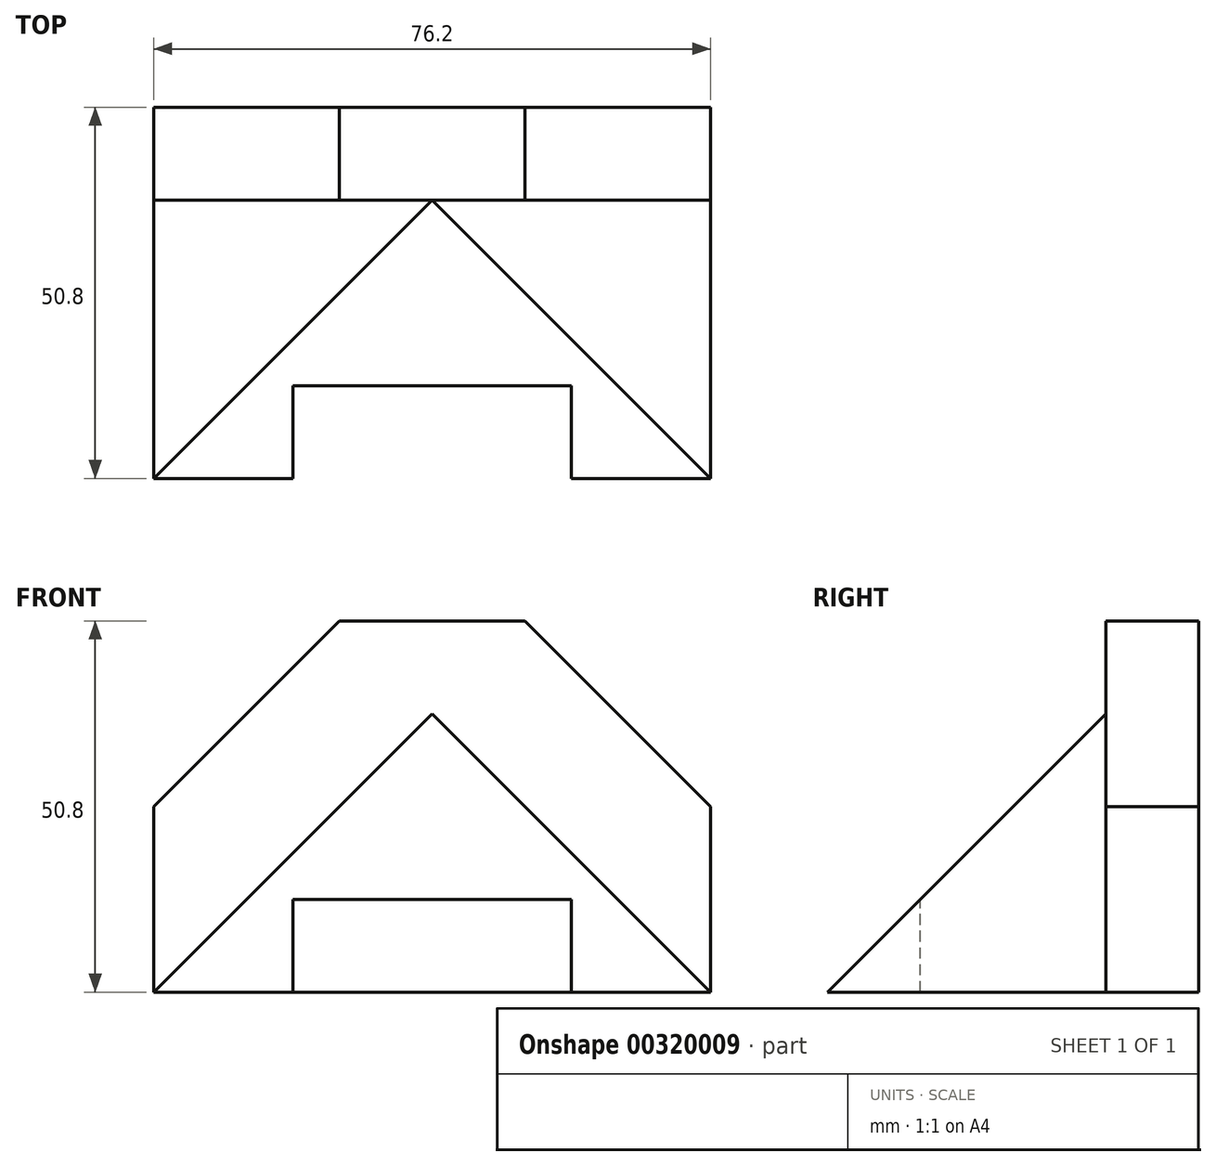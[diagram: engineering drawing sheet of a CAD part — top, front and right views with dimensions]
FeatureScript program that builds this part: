
annotation { "Feature Type Name" : "Feature", "Feature Type Description" : "" }
export const myFeature = defineFeature(function(context is Context, id is Id, definition is map)
    precondition{}
    {
        {
            var Q0;
            Q0=qCreatedBy(makeId("Front.planeOp"),FACE);
            var sketch = newSketch(context, id + "F0", { "sketchPlane" : qUnion([Q0])});
            skLineSegment(sketch, "E0.bottom", {"start": v(0, 0) * mm, "end": v(76.2, 0) * mm});
            skLineSegment(sketch, "E0.top", {"start": v(0, 50.8) * mm, "end": v(76.2, 50.8) * mm});
            skLineSegment(sketch, "E0.left", {"start": v(0, 0) * mm, "end": v(0, 50.8) * mm});
            skLineSegment(sketch, "E0.right", {"start": v(76.2, 0) * mm, "end": v(76.2, 50.8) * mm});
            skLineSegment(sketch, "E1", {"start": v(76.2, 0) * mm, "end": v(38.1, 38.1) * mm});
            skLineSegment(sketch, "E2", {"start": v(38.1, 38.1) * mm, "end": v(0, 0) * mm});
            skSolve(sketch);
        }
        {
            var Q0;
            Q0 = qSketchRegion(id + "F0", true);
            extrude(context, id + "F1", {"entities" : qUnion([Q0]), "oppositeDirection" : true, "depth" : 50.8 * mm});
        }
        {
            var Q0;
            Q0=makeQuery(id+"F1.opExtrude","SWEPT_FACE",FACE,{"disambiguationData":[OSD([sQuery(id+"F0.wireOp",EDGE,"E0.top")])]});
            var sketch = newSketch(context, id + "F2", { "sketchPlane" : qUnion([Q0])});
            skLineSegment(sketch, "E3", {"start": v(19.05, 0) * mm, "end": v(19.05, 12.7) * mm});
            skLineSegment(sketch, "E4", {"start": v(19.05, 12.7) * mm, "end": v(57.15, 12.7) * mm});
            skLineSegment(sketch, "E5", {"start": v(57.15, 12.7) * mm, "end": v(57.15, 0) * mm});
            skSolve(sketch);
        }
        {
            var Q0;
            {var subQ0=sQuery(id+"F2.wireOp",EDGE,"E3");Q0=makeQuery(id+"F2.imprint","IMPRINT",FACE,{"disambiguationData":[TD([[makeQuery(id+"F2.imprint","IMPRINT",EDGE,{"derivedFrom":subQ0}),-1.0]])]});}
            extrude(context, id + "F3", {"entities" : qUnion([Q0]), "operationType" : NewBodyOperationType.REMOVE, "oppositeDirection" : true, "depth" : 76.2 * mm});
        }
        {
            var Q0;
            {var subQ0=sQuery(id+"F0.wireOp",EDGE,"E0.right");Q0=makeQuery(id+"F0.imprint","IMPRINT",FACE,{"disambiguationData":[TD([[makeQuery(id+"F0.imprint","IMPRINT",EDGE,{"derivedFrom":subQ0}),1.0]])]});}
            var Q1;
            {var subQ0=sQuery(id+"F0.wireOp",EDGE,"E0.left");Q1=makeQuery(id+"F0.imprint","IMPRINT",FACE,{"disambiguationData":[TD([[makeQuery(id+"F0.imprint","IMPRINT",EDGE,{"derivedFrom":subQ0}),-1.0]])]});}
            extrude(context, id + "F4", {"entities" : qUnion([Q0, Q1]), "operationType" : NewBodyOperationType.REMOVE, "oppositeDirection" : true, "depth" : 38.1 * mm});
        }
        {
            var Q0;
            Q0=makeQuery(id+"F1.opExtrude","SWEPT_FACE",FACE,{"disambiguationData":[OSD([sQuery(id+"F0.wireOp",EDGE,"E0.right")])]});
            var sketch = newSketch(context, id + "F5", { "sketchPlane" : qUnion([Q0])});
            skLineSegment(sketch, "E6", {"start": v(38.1, 38.1) * mm, "end": v(0, 0) * mm});
            skLineSegment(sketch, "E7", {"start": v(38.1, 50.8) * mm, "end": v(12.7, 50.8) * mm});
            skLineSegment(sketch, "E8", {"start": v(12.7, 50.8) * mm, "end": v(12.7, 25.4) * mm});
            skLineSegment(sketch, "E9", {"start": v(12.7, 25.4) * mm, "end": v(0, 25.4) * mm});
            skLineSegment(sketch, "E10", {"start": v(0, 25.4) * mm, "end": v(0, 0) * mm});
            skSolve(sketch);
        }
        {
            var Q0;
            {var subQ1=sQuery(id+"F5.wireOp",EDGE,"E6");Q0=makeQuery(id+"F5.imprint","IMPRINT",FACE,{"disambiguationData":[TD([[makeQuery(id+"F5.imprint","IMPRINT",EDGE,{"derivedFrom":subQ1}),-1.0]])]});}
            extrude(context, id + "F6", {"entities" : qUnion([Q0]), "operationType" : NewBodyOperationType.REMOVE, "oppositeDirection" : true, "depth" : 101.6 * mm});
        }
        {
            var Q0;
            Q0=makeQuery(id+"F4.boolean.opBoolean","COPY",FACE,{"derivedFrom":makeQuery(id+"F4.opExtrude","CAP_FACE",FACE,{"disambiguationData":[OSD([sQuery(id+"F0.wireOp",EDGE,"E0.top"),sQuery(id+"F0.wireOp",EDGE,"E0.left"),sQuery(id+"F0.wireOp",EDGE,"E0.right"),sQuery(id+"F0.wireOp",EDGE,"E1"),sQuery(id+"F0.wireOp",EDGE,"E2")])],"isStart":false})});
            var sketch = newSketch(context, id + "F7", { "sketchPlane" : qUnion([Q0])});
            skLineSegment(sketch, "E11", {"start": v(76.2, 25.4) * mm, "end": v(50.8, 50.8) * mm});
            skLineSegment(sketch, "E12", {"start": v(25.4, 50.8) * mm, "end": v(0, 25.4) * mm});
            skSolve(sketch);
        }
        {
            var Q0;
            {var subQ0=sQuery(id+"F7.wireOp",EDGE,"E11");Q0=makeQuery(id+"F7.imprint","IMPRINT",FACE,{"disambiguationData":[TD([[makeQuery(id+"F7.imprint","IMPRINT",EDGE,{"derivedFrom":subQ0}),-1.0]])]});}
            var Q1;
            {var subQ0=sQuery(id+"F7.wireOp",EDGE,"E12");Q1=makeQuery(id+"F7.imprint","IMPRINT",FACE,{"disambiguationData":[TD([[makeQuery(id+"F7.imprint","IMPRINT",EDGE,{"derivedFrom":subQ0}),-1.0]])]});}
            extrude(context, id + "F8", {"entities" : qUnion([Q0, Q1]), "operationType" : NewBodyOperationType.REMOVE, "oppositeDirection" : true, "depth" : 25.4 * mm});
        }
    });
